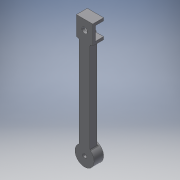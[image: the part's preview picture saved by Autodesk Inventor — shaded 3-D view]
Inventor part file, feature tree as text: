
AUTODESK INVENTOR PART (.ipt)
format: ipt  version: 2019 (Build 230136000, 136)  size: 180,736 bytes
history: native  units: mm
features: extrude x6, sketch x6, other x4, fillet x3, reference x2
ambient origin geometry x8: Origin, YZ Plane, XZ Plane, XY Plane, X Axis, Y Axis, Z Axis, Center Point
bodies: Solid1 (feature_tree)
feature tree (21):
  extrude  "Extrusion1"  Depth=8.0mm
  extrude  "Extrusion2"  Depth=8.0mm
  extrude  "Extrusion3"  Depth=80.0mm
  extrude  "Extrusion4"  Depth=1.0mm
  fillet  "Fillet1"  Radius=4.1mm
  extrude  "Extrusion5"  Depth=3.0mm
  fillet  "Fillet2"  Radius=2.5mm
  fillet  "Fillet3"  Radius=3.0mm
  extrude  "Extrusion6"  Depth=2.0mm
  sketch  "Sketch1"  dims[d0=8.0mm d1=14.0mm]
  sketch  "Sketch2"  dims[d2=8.0mm d3=12.0mm]
  sketch  "Sketch3"  dims[d4=14.0mm d6=80.0mm]
  sketch  "Sketch4"  dims[d7=3.0mm d8=1.0mm d9=4.1mm]
  sketch  "Sketch5"  dims[d10=8.0mm d11=0.0mm d12=8.1mm d13=2.5mm d14=0.0mm d15=3.0mm d16=0.0mm]
  reference  "Reference1"
  reference  "Reference2"
  sketch  "Sketch6"  dims[d17=2.0mm d18=2.0mm d19=6.0mm d20=0.0mm d21=1.0mm d22=1.0mm d23=2.0mm d24=0.0mm d25=0.1mm d26=0.4mm d27=1.0mm d28=0.0mm]
  parser-record x1  (decoder bookkeeping rows leaked as tree rows — omitted from the tree; the rows remain in map.json)
  other  "Kinematics.iam"
  other  "Motor-GM15BY:2"
  other  "Motor-Body:1"
note: 1 file-system path scrubbed to <path> (originals preserved in map.json)
